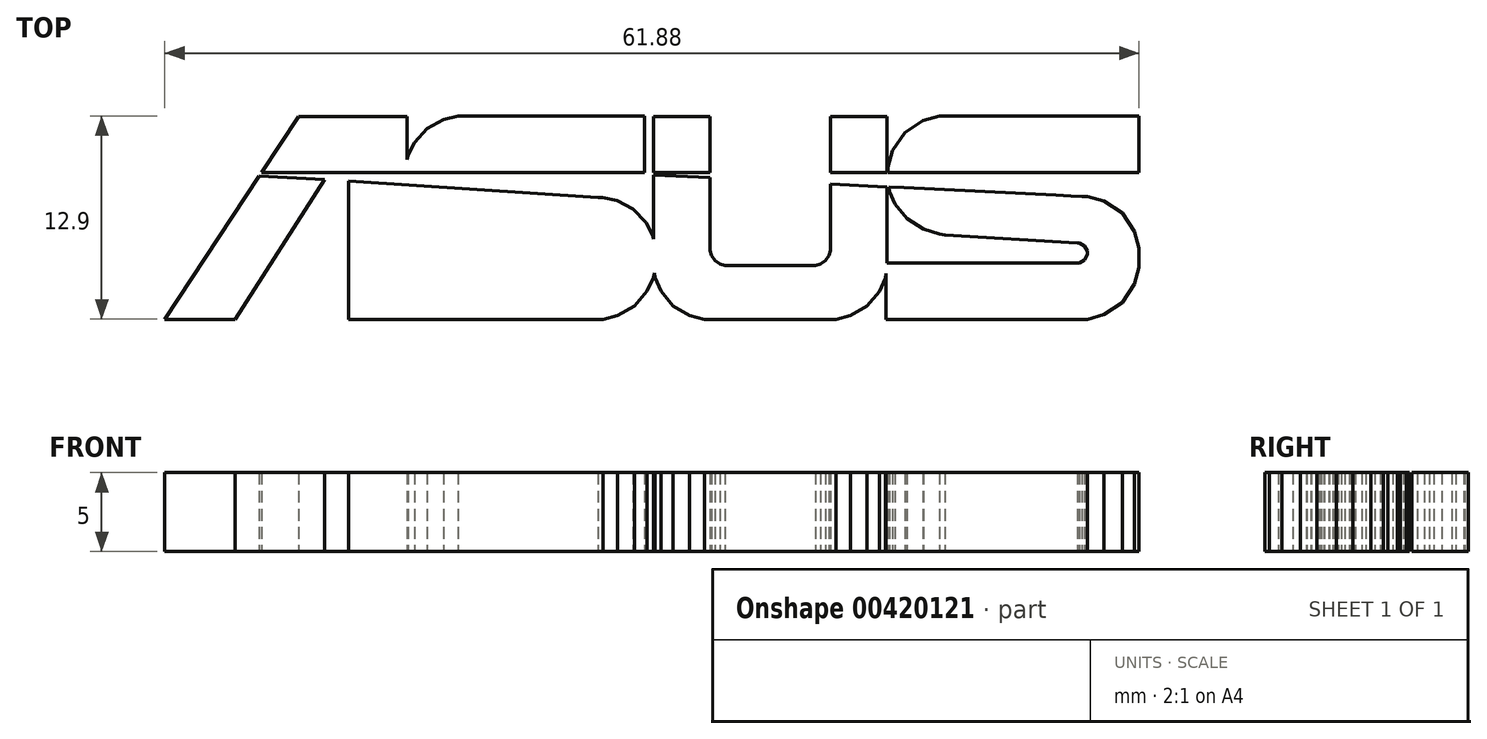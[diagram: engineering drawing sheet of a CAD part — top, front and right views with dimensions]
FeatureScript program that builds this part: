
annotation { "Feature Type Name" : "Feature", "Feature Type Description" : "" }
export const myFeature = defineFeature(function(context is Context, id is Id, definition is map)
    precondition{}
    {
        {
            var Q0;
            Q0=qCreatedBy(makeId("Top.planeOp"),FACE);
            var sketch = newSketch(context, id + "F0", { "sketchPlane" : qUnion([Q0])});
            skLineSegment(sketch, "E0", {"start": v(1.58, 6.43) * mm, "end": v(1.63, 6.43) * mm});
            skLineSegment(sketch, "E1", {"start": v(1.63, 6.43) * mm, "end": v(1.63, 2.87) * mm});
            skLineSegment(sketch, "E2", {"start": v(1.63, 2.87) * mm, "end": v(-1.96, 2.87) * mm});
            skLineSegment(sketch, "E3", {"start": v(-1.96, 2.87) * mm, "end": v(-1.96, 6.43) * mm});
            skLineSegment(sketch, "E4", {"start": v(-1.96, 6.43) * mm, "end": v(1.58, 6.43) * mm});
            skLineSegment(sketch, "E5", {"start": v(-14.08, -1.1) * mm, "end": v(-5.76, -1.61) * mm});
            skLineSegment(sketch, "E6", {"start": v(-5.76, -1.61) * mm, "end": v(-5.65, -1.61) * mm});
            skLineSegment(sketch, "E7", {"start": v(-5.65, -1.61) * mm, "end": v(-5.31, -1.8) * mm});
            skLineSegment(sketch, "E8", {"start": v(-5.31, -1.8) * mm, "end": v(-5.13, -2.13) * mm});
            skLineSegment(sketch, "E9", {"start": v(-5.13, -2.13) * mm, "end": v(-5.13, -2.24) * mm});
            skLineSegment(sketch, "E10", {"start": v(-5.13, -2.24) * mm, "end": v(-5.13, -2.35) * mm});
            skLineSegment(sketch, "E11", {"start": v(-5.13, -2.35) * mm, "end": v(-5.31, -2.69) * mm});
            skLineSegment(sketch, "E12", {"start": v(-5.31, -2.69) * mm, "end": v(-5.65, -2.87) * mm});
            skLineSegment(sketch, "E13", {"start": v(-5.65, -2.87) * mm, "end": v(-5.76, -2.87) * mm});
            skLineSegment(sketch, "E14", {"start": v(-5.76, -2.87) * mm, "end": v(-17.62, -2.87) * mm});
            skLineSegment(sketch, "E15", {"start": v(-17.62, -2.87) * mm, "end": v(-17.62, 1.77) * mm});
            skLineSegment(sketch, "E16", {"start": v(-17.62, 2.08) * mm, "end": v(-17.55, 1.5) * mm});
            skLineSegment(sketch, "E17", {"start": v(-17.55, 1.5) * mm, "end": v(-17.18, 0.75) * mm});
            skLineSegment(sketch, "E18", {"start": v(-17.18, 0.75) * mm, "end": v(-16.43, -0.1) * mm});
            skLineSegment(sketch, "E19", {"start": v(-16.43, -0.1) * mm, "end": v(-15.39, -0.74) * mm});
            skLineSegment(sketch, "E20", {"start": v(-15.39, -0.74) * mm, "end": v(-14.41, -1.05) * mm});
            skLineSegment(sketch, "E21", {"start": v(-14.41, -1.05) * mm, "end": v(-14.08, -1.1) * mm});
            skLineSegment(sketch, "E22", {"start": v(-17.62, -6.45) * mm, "end": v(-5.5, -6.45) * mm});
            skLineSegment(sketch, "E23", {"start": v(-5.5, -6.45) * mm, "end": v(-5.18, -6.45) * mm});
            skLineSegment(sketch, "E24", {"start": v(-5.18, -6.45) * mm, "end": v(-4.23, -6.23) * mm});
            skLineSegment(sketch, "E25", {"start": v(-4.23, -6.23) * mm, "end": v(-3.16, -5.6) * mm});
            skLineSegment(sketch, "E26", {"start": v(-3.16, -5.6) * mm, "end": v(-2.36, -4.67) * mm});
            skLineSegment(sketch, "E27", {"start": v(-2.36, -4.67) * mm, "end": v(-1.97, -3.8) * mm});
            skLineSegment(sketch, "E28", {"start": v(-1.97, -3.8) * mm, "end": v(-1.91, -3.5) * mm});
            skLineSegment(sketch, "E29", {"start": v(-1.91, -3.5) * mm, "end": v(-1.86, -3.8) * mm});
            skLineSegment(sketch, "E30", {"start": v(-1.86, -3.8) * mm, "end": v(-1.5, -4.67) * mm});
            skLineSegment(sketch, "E31", {"start": v(-1.5, -4.67) * mm, "end": v(-0.71, -5.6) * mm});
            skLineSegment(sketch, "E32", {"start": v(-0.71, -5.6) * mm, "end": v(0.34, -6.23) * mm});
            skLineSegment(sketch, "E33", {"start": v(0.34, -6.23) * mm, "end": v(1.27, -6.45) * mm});
            skLineSegment(sketch, "E34", {"start": v(1.27, -6.45) * mm, "end": v(1.58, -6.45) * mm});
            skLineSegment(sketch, "E35", {"start": v(1.58, -6.45) * mm, "end": v(9.33, -6.45) * mm});
            skLineSegment(sketch, "E36", {"start": v(9.33, -6.45) * mm, "end": v(9.64, -6.45) * mm});
            skLineSegment(sketch, "E37", {"start": v(9.64, -6.45) * mm, "end": v(10.56, -6.23) * mm});
            skLineSegment(sketch, "E38", {"start": v(10.56, -6.23) * mm, "end": v(11.6, -5.62) * mm});
            skLineSegment(sketch, "E39", {"start": v(11.6, -5.62) * mm, "end": v(12.39, -4.7) * mm});
            skLineSegment(sketch, "E40", {"start": v(12.39, -4.7) * mm, "end": v(12.76, -3.84) * mm});
            skLineSegment(sketch, "E41", {"start": v(12.76, -3.84) * mm, "end": v(12.82, -3.54) * mm});
            skLineSegment(sketch, "E42", {"start": v(12.82, -3.54) * mm, "end": v(12.82, -6.45) * mm});
            skLineSegment(sketch, "E43", {"start": v(12.82, -6.45) * mm, "end": v(25.24, -6.45) * mm});
            skLineSegment(sketch, "E44", {"start": v(25.24, -6.45) * mm, "end": v(25.6, -6.45) * mm});
            skLineSegment(sketch, "E45", {"start": v(25.6, -6.45) * mm, "end": v(26.65, -6.17) * mm});
            skLineSegment(sketch, "E46", {"start": v(26.65, -6.17) * mm, "end": v(27.81, -5.38) * mm});
            skLineSegment(sketch, "E47", {"start": v(27.81, -5.38) * mm, "end": v(28.6, -4.22) * mm});
            skLineSegment(sketch, "E48", {"start": v(28.6, -4.22) * mm, "end": v(28.88, -3.16) * mm});
            skLineSegment(sketch, "E49", {"start": v(28.88, -3.16) * mm, "end": v(28.88, -2.8) * mm});
            skLineSegment(sketch, "E50", {"start": v(28.88, -2.8) * mm, "end": v(28.88, -2.3) * mm});
            skLineSegment(sketch, "E51", {"start": v(28.88, -2.3) * mm, "end": v(28.88, -1.94) * mm});
            skLineSegment(sketch, "E52", {"start": v(28.88, -1.94) * mm, "end": v(28.6, -0.87) * mm});
            skLineSegment(sketch, "E53", {"start": v(28.6, -0.87) * mm, "end": v(27.81, 0.29) * mm});
            skLineSegment(sketch, "E54", {"start": v(27.81, 0.29) * mm, "end": v(26.65, 1.07) * mm});
            skLineSegment(sketch, "E55", {"start": v(26.65, 1.07) * mm, "end": v(25.6, 1.35) * mm});
            skLineSegment(sketch, "E56", {"start": v(25.6, 1.35) * mm, "end": v(25.24, 1.35) * mm});
            skLineSegment(sketch, "E57", {"start": v(25.24, 1.35) * mm, "end": v(24.56, 1.39) * mm});
            skLineSegment(sketch, "E58", {"start": v(24.56, 1.39) * mm, "end": v(23.59, 1.43) * mm});
            skLineSegment(sketch, "E59", {"start": v(23.59, 1.43) * mm, "end": v(13.94, 1.9) * mm});
            skLineSegment(sketch, "E60", {"start": v(13.94, 1.9) * mm, "end": v(12.98, 1.95) * mm});
            skLineSegment(sketch, "E61", {"start": v(12.98, 1.95) * mm, "end": v(13.03, 1.67) * mm});
            skLineSegment(sketch, "E62", {"start": v(13.03, 1.67) * mm, "end": v(13.38, 0.87) * mm});
            skLineSegment(sketch, "E63", {"start": v(13.38, 0.87) * mm, "end": v(14.13, -0.04) * mm});
            skLineSegment(sketch, "E64", {"start": v(14.13, -0.04) * mm, "end": v(15.2, -0.72) * mm});
            skLineSegment(sketch, "E65", {"start": v(15.2, -0.72) * mm, "end": v(16.21, -1.05) * mm});
            skLineSegment(sketch, "E66", {"start": v(16.21, -1.05) * mm, "end": v(16.56, -1.1) * mm});
            skLineSegment(sketch, "E67", {"start": v(16.56, -1.1) * mm, "end": v(24.97, -1.61) * mm});
            skLineSegment(sketch, "E68", {"start": v(24.97, -1.61) * mm, "end": v(25.08, -1.61) * mm});
            skLineSegment(sketch, "E69", {"start": v(25.08, -1.61) * mm, "end": v(25.42, -1.8) * mm});
            skLineSegment(sketch, "E70", {"start": v(25.42, -1.8) * mm, "end": v(25.6, -2.13) * mm});
            skLineSegment(sketch, "E71", {"start": v(25.6, -2.13) * mm, "end": v(25.6, -2.24) * mm});
            skLineSegment(sketch, "E72", {"start": v(25.6, -2.24) * mm, "end": v(25.6, -2.35) * mm});
            skLineSegment(sketch, "E73", {"start": v(25.6, -2.35) * mm, "end": v(25.42, -2.69) * mm});
            skLineSegment(sketch, "E74", {"start": v(25.42, -2.69) * mm, "end": v(25.08, -2.87) * mm});
            skLineSegment(sketch, "E75", {"start": v(25.08, -2.87) * mm, "end": v(24.97, -2.87) * mm});
            skLineSegment(sketch, "E76", {"start": v(24.97, -2.87) * mm, "end": v(12.88, -2.87) * mm});
            skLineSegment(sketch, "E77", {"start": v(12.88, -2.87) * mm, "end": v(12.88, 1.95) * mm});
            skLineSegment(sketch, "E78", {"start": v(12.88, 1.95) * mm, "end": v(9.28, 2.14) * mm});
            skLineSegment(sketch, "E79", {"start": v(9.28, 2.14) * mm, "end": v(9.28, -1.99) * mm});
            skLineSegment(sketch, "E80", {"start": v(9.28, -1.99) * mm, "end": v(9.28, -2.09) * mm});
            skLineSegment(sketch, "E81", {"start": v(9.28, -2.09) * mm, "end": v(9.2, -2.4) * mm});
            skLineSegment(sketch, "E82", {"start": v(9.2, -2.4) * mm, "end": v(8.97, -2.73) * mm});
            skLineSegment(sketch, "E83", {"start": v(8.97, -2.73) * mm, "end": v(8.64, -2.95) * mm});
            skLineSegment(sketch, "E84", {"start": v(8.64, -2.95) * mm, "end": v(8.33, -3.04) * mm});
            skLineSegment(sketch, "E85", {"start": v(8.33, -3.04) * mm, "end": v(8.23, -3.04) * mm});
            skLineSegment(sketch, "E86", {"start": v(8.23, -3.04) * mm, "end": v(2.68, -3.04) * mm});
            skLineSegment(sketch, "E87", {"start": v(2.68, -3.04) * mm, "end": v(2.58, -3.04) * mm});
            skLineSegment(sketch, "E88", {"start": v(2.58, -3.04) * mm, "end": v(2.28, -2.95) * mm});
            skLineSegment(sketch, "E89", {"start": v(2.28, -2.95) * mm, "end": v(1.94, -2.73) * mm});
            skLineSegment(sketch, "E90", {"start": v(1.94, -2.73) * mm, "end": v(1.72, -2.4) * mm});
            skLineSegment(sketch, "E91", {"start": v(1.72, -2.4) * mm, "end": v(1.63, -2.09) * mm});
            skLineSegment(sketch, "E92", {"start": v(1.63, -2.09) * mm, "end": v(1.63, -1.99) * mm});
            skLineSegment(sketch, "E93", {"start": v(1.63, -1.99) * mm, "end": v(1.63, 2.53) * mm});
            skLineSegment(sketch, "E94", {"start": v(1.63, 2.53) * mm, "end": v(-1.96, 2.72) * mm});
            skLineSegment(sketch, "E95", {"start": v(-1.96, 2.72) * mm, "end": v(-1.96, -1.37) * mm});
            skLineSegment(sketch, "E96", {"start": v(-1.96, -1.37) * mm, "end": v(-2.04, -1.1) * mm});
            skLineSegment(sketch, "E97", {"start": v(-2.04, -1.1) * mm, "end": v(-2.45, -0.3) * mm});
            skLineSegment(sketch, "E98", {"start": v(-2.45, -0.3) * mm, "end": v(-3.25, 0.54) * mm});
            skLineSegment(sketch, "E99", {"start": v(-3.25, 0.54) * mm, "end": v(-4.29, 1.1) * mm});
            skLineSegment(sketch, "E100", {"start": v(-4.29, 1.1) * mm, "end": v(-5.2, 1.3) * mm});
            skLineSegment(sketch, "E101", {"start": v(-5.2, 1.3) * mm, "end": v(-5.5, 1.3) * mm});
            skLineSegment(sketch, "E102", {"start": v(-5.5, 1.3) * mm, "end": v(-21.34, 2.33) * mm});
            skLineSegment(sketch, "E103", {"start": v(-21.34, 2.33) * mm, "end": v(-21.34, -6.45) * mm});
            skLineSegment(sketch, "E104", {"start": v(-21.34, -6.45) * mm, "end": v(-17.91, -6.45) * mm});
            skLineSegment(sketch, "E105", {"start": v(-17.91, -6.45) * mm, "end": v(-17.62, -6.45) * mm});
            skLineSegment(sketch, "E106", {"start": v(-2.54, 2.87) * mm, "end": v(-2.54, 6.45) * mm});
            skLineSegment(sketch, "E107", {"start": v(-2.54, 6.45) * mm, "end": v(-14.08, 6.45) * mm});
            skLineSegment(sketch, "E108", {"start": v(-14.08, 6.45) * mm, "end": v(-14.38, 6.45) * mm});
            skLineSegment(sketch, "E109", {"start": v(-14.38, 6.45) * mm, "end": v(-15.3, 6.24) * mm});
            skLineSegment(sketch, "E110", {"start": v(-15.3, 6.24) * mm, "end": v(-16.34, 5.66) * mm});
            skLineSegment(sketch, "E111", {"start": v(-16.34, 5.66) * mm, "end": v(-17.14, 4.78) * mm});
            skLineSegment(sketch, "E112", {"start": v(-17.14, 4.78) * mm, "end": v(-17.55, 3.97) * mm});
            skLineSegment(sketch, "E113", {"start": v(-17.55, 3.97) * mm, "end": v(-17.62, 3.68) * mm});
            skLineSegment(sketch, "E114", {"start": v(-17.62, 3.68) * mm, "end": v(-17.62, 6.43) * mm});
            skLineSegment(sketch, "E115", {"start": v(-17.62, 6.43) * mm, "end": v(-24.5, 6.43) * mm});
            skLineSegment(sketch, "E116", {"start": v(-24.5, 6.43) * mm, "end": v(-26.85, 2.87) * mm});
            skLineSegment(sketch, "E117", {"start": v(-26.85, 2.87) * mm, "end": v(-17.72, 2.87) * mm});
            skLineSegment(sketch, "E118", {"start": v(-17.72, 2.87) * mm, "end": v(-2.54, 2.87) * mm});
            skLineSegment(sketch, "E119", {"start": v(-22.86, 2.42) * mm, "end": v(-28.55, -6.45) * mm});
            skLineSegment(sketch, "E120", {"start": v(-28.55, -6.45) * mm, "end": v(-33, -6.45) * mm});
            skLineSegment(sketch, "E121", {"start": v(-33, -6.45) * mm, "end": v(-27, 2.66) * mm});
            skLineSegment(sketch, "E122", {"start": v(-27, 2.66) * mm, "end": v(-22.86, 2.42) * mm});
            skLineSegment(sketch, "E123", {"start": v(28.88, 2.87) * mm, "end": v(28.88, 6.45) * mm});
            skLineSegment(sketch, "E124", {"start": v(28.88, 6.45) * mm, "end": v(16.56, 6.45) * mm});
            skLineSegment(sketch, "E125", {"start": v(16.56, 6.45) * mm, "end": v(16.2, 6.45) * mm});
            skLineSegment(sketch, "E126", {"start": v(16.2, 6.45) * mm, "end": v(15.16, 6.17) * mm});
            skLineSegment(sketch, "E127", {"start": v(15.16, 6.17) * mm, "end": v(14, 5.4) * mm});
            skLineSegment(sketch, "E128", {"start": v(14, 5.4) * mm, "end": v(13.22, 4.27) * mm});
            skLineSegment(sketch, "E129", {"start": v(13.22, 4.27) * mm, "end": v(12.92, 3.22) * mm});
            skLineSegment(sketch, "E130", {"start": v(12.92, 3.22) * mm, "end": v(12.92, 2.87) * mm});
            skLineSegment(sketch, "E131", {"start": v(12.92, 2.87) * mm, "end": v(28.88, 2.87) * mm});
            skLineSegment(sketch, "E132", {"start": v(9.28, 2.87) * mm, "end": v(9.28, 6.43) * mm});
            skLineSegment(sketch, "E133", {"start": v(9.28, 6.43) * mm, "end": v(9.33, 6.43) * mm});
            skLineSegment(sketch, "E134", {"start": v(9.33, 6.43) * mm, "end": v(12.88, 6.43) * mm});
            skLineSegment(sketch, "E135", {"start": v(12.88, 6.43) * mm, "end": v(12.88, 2.87) * mm});
            skLineSegment(sketch, "E136", {"start": v(12.88, 2.87) * mm, "end": v(9.28, 2.87) * mm});
            skLineSegment(sketch, "E137", {"start": v(12.82, -3.54) * mm, "end": v(12.88, -2.87) * mm});
            skLineSegment(sketch, "E138", {"start": v(-1.91, -3.5) * mm, "end": v(-1.96, -1.37) * mm});
            skLineSegment(sketch, "E139", {"start": v(-17.62, 1.77) * mm, "end": v(-17.62, 2.08) * mm});
            skLineSegment(sketch, "E140", {"start": v(-17.62, 3.68) * mm, "end": v(-17.62, 2.87) * mm});
            skLineSegment(sketch, "E141", {"start": v(-17.62, 1.77) * mm, "end": v(-17.62, -2.87) * mm});
            skLineSegment(sketch, "E142", {"start": v(-5.76, -2.87) * mm, "end": v(-5.65, -2.87) * mm});
            skLineSegment(sketch, "E143", {"start": v(-5.31, -2.69) * mm, "end": v(-5.13, -2.35) * mm});
            skLineSegment(sketch, "E144", {"start": v(-5.13, -2.24) * mm, "end": v(-5.13, -2.13) * mm});
            skLineSegment(sketch, "E145", {"start": v(-5.31, -1.8) * mm, "end": v(-5.65, -1.61) * mm});
            skLineSegment(sketch, "E146", {"start": v(-5.76, -1.61) * mm, "end": v(-14.08, -1.1) * mm});
            skLineSegment(sketch, "E147", {"start": v(-14.41, -1.05) * mm, "end": v(-15.39, -0.74) * mm});
            skLineSegment(sketch, "E148", {"start": v(-16.43, -0.1) * mm, "end": v(-17.18, 0.75) * mm});
            skLineSegment(sketch, "E149", {"start": v(-17.55, 1.5) * mm, "end": v(-17.58, 1.77) * mm});
            skLineSegment(sketch, "E150", {"start": v(-17.62, -2.87) * mm, "end": v(-17.62, -6.45) * mm});
            skSolve(sketch);
        }
        {
            var Q0;
            Q0=makeQuery(id+"F0.imprint","IMPRINT",FACE,{"disambiguationData":[TD([[makeQuery(id+"F0.imprint","IMPRINT",EDGE,{"derivedFrom":sQuery(id+"F0.wireOp",EDGE,"E0")}),-1.0]])]});
            var Q1;
            Q1=makeQuery(id+"F0.imprint","IMPRINT",FACE,{"disambiguationData":[TD([[makeQuery(id+"F0.imprint","IMPRINT",EDGE,{"derivedFrom":sQuery(id+"F0.wireOp",EDGE,"E119")}),-1.0]])]});
            var Q2;
            Q2=makeQuery(id+"F0.imprint","IMPRINT",FACE,{"disambiguationData":[TD([[makeQuery(id+"F0.imprint","IMPRINT",EDGE,{"derivedFrom":sQuery(id+"F0.wireOp",EDGE,"E123")}),1.0]])]});
            var Q3;
            Q3=makeQuery(id+"F0.imprint","IMPRINT",FACE,{"disambiguationData":[TD([[makeQuery(id+"F0.imprint","IMPRINT",EDGE,{"derivedFrom":sQuery(id+"F0.wireOp",EDGE,"E132")}),-1.0]])]});
            var Q4;
            Q4=makeQuery(id+"F0.imprint","IMPRINT",FACE,{"disambiguationData":[TD([[makeQuery(id+"F0.imprint","IMPRINT",EDGE,{"derivedFrom":sQuery(id+"F0.wireOp",EDGE,"E42")}),1.0]])]});
            var Q5;
            {var subQ1=sQuery(id+"F0.wireOp",EDGE,"E103");Q5=makeQuery(id+"F0.imprint","IMPRINT",FACE,{"disambiguationData":[TD([[makeQuery(id+"F0.imprint","IMPRINT",EDGE,{"derivedFrom":subQ1}),1.0]])]});}
            var Q6;
            {var subQ1=sQuery(id+"F0.wireOp",EDGE,"E106");Q6=makeQuery(id+"F0.imprint","IMPRINT",FACE,{"disambiguationData":[TD([[makeQuery(id+"F0.imprint","IMPRINT",EDGE,{"derivedFrom":subQ1}),1.0]])]});}
            var Q7;
            Q7=makeQuery(id+"F0.imprint","IMPRINT",FACE,{"disambiguationData":[TD([[makeQuery(id+"F0.imprint","IMPRINT",EDGE,{"derivedFrom":sQuery(id+"F0.wireOp",EDGE,"E114")}),1.0]])]});
            var Q8;
            Q8=makeQuery(id+"F0.imprint","IMPRINT",FACE,{"disambiguationData":[TD([[makeQuery(id+"F0.imprint","IMPRINT",EDGE,{"derivedFrom":sQuery(id+"F0.wireOp",EDGE,"E29")}),1.0]])]});
            var Q9;
            {var subQ4=sQuery(id+"F0.wireOp",EDGE,"E22");Q9=makeQuery(id+"F0.imprint","IMPRINT",FACE,{"disambiguationData":[TD([[makeQuery(id+"F0.imprint","IMPRINT",EDGE,{"derivedFrom":subQ4}),1.0]])]});}
            extrude(context, id + "F1", {"entities" : qUnion([Q0, Q1, Q2, Q3, Q4, Q5, Q6, Q7, Q8, Q9]), "depth" : 5 * mm});
        }
        {
            var Q0;
            Q0=sQuery(id+"F0.wireOp",EDGE,"E146");
            var Q1;
            Q1=sQuery(id+"F0.wireOp",EDGE,"E21");
            var Q2;
            Q2=sQuery(id+"F0.wireOp",EDGE,"E20");
            var Q3;
            Q3=sQuery(id+"F0.wireOp",EDGE,"E19");
            var Q4;
            Q4=sQuery(id+"F0.wireOp",EDGE,"E18");
            var Q5;
            Q5=sQuery(id+"F0.wireOp",EDGE,"E17");
            var Q6;
            Q6=sQuery(id+"F0.wireOp",EDGE,"E16");
            var Q7;
            Q7=sQuery(id+"F0.wireOp",EDGE,"E139");
            var Q8;
            Q8=sQuery(id+"F0.wireOp",EDGE,"E15");
            var Q9;
            Q9=sQuery(id+"F0.wireOp",EDGE,"E14");
            var Q10;
            Q10=sQuery(id+"F0.wireOp",EDGE,"E13");
            var Q11;
            Q11=sQuery(id+"F0.wireOp",EDGE,"E12");
            var Q12;
            Q12=sQuery(id+"F0.wireOp",EDGE,"E11");
            var Q13;
            Q13=sQuery(id+"F0.wireOp",EDGE,"E6");
            var Q14;
            Q14=sQuery(id+"F0.wireOp",EDGE,"E145");
            var Q15;
            Q15=sQuery(id+"F0.wireOp",EDGE,"E8");
            var Q16;
            Q16=sQuery(id+"F0.wireOp",EDGE,"E144");
            var Q17;
            Q17=sQuery(id+"F0.wireOp",EDGE,"E10");
            extrude(context, id + "F2", {"bodyType" : ToolBodyType.SURFACE, "surfaceEntities" : qUnion([Q0, Q1, Q2, Q3, Q4, Q5, Q6, Q7, Q8, Q9, Q10, Q11, Q12, Q13, Q14, Q15, Q16, Q17]), "depth" : 10 * mm});
        }
    });
